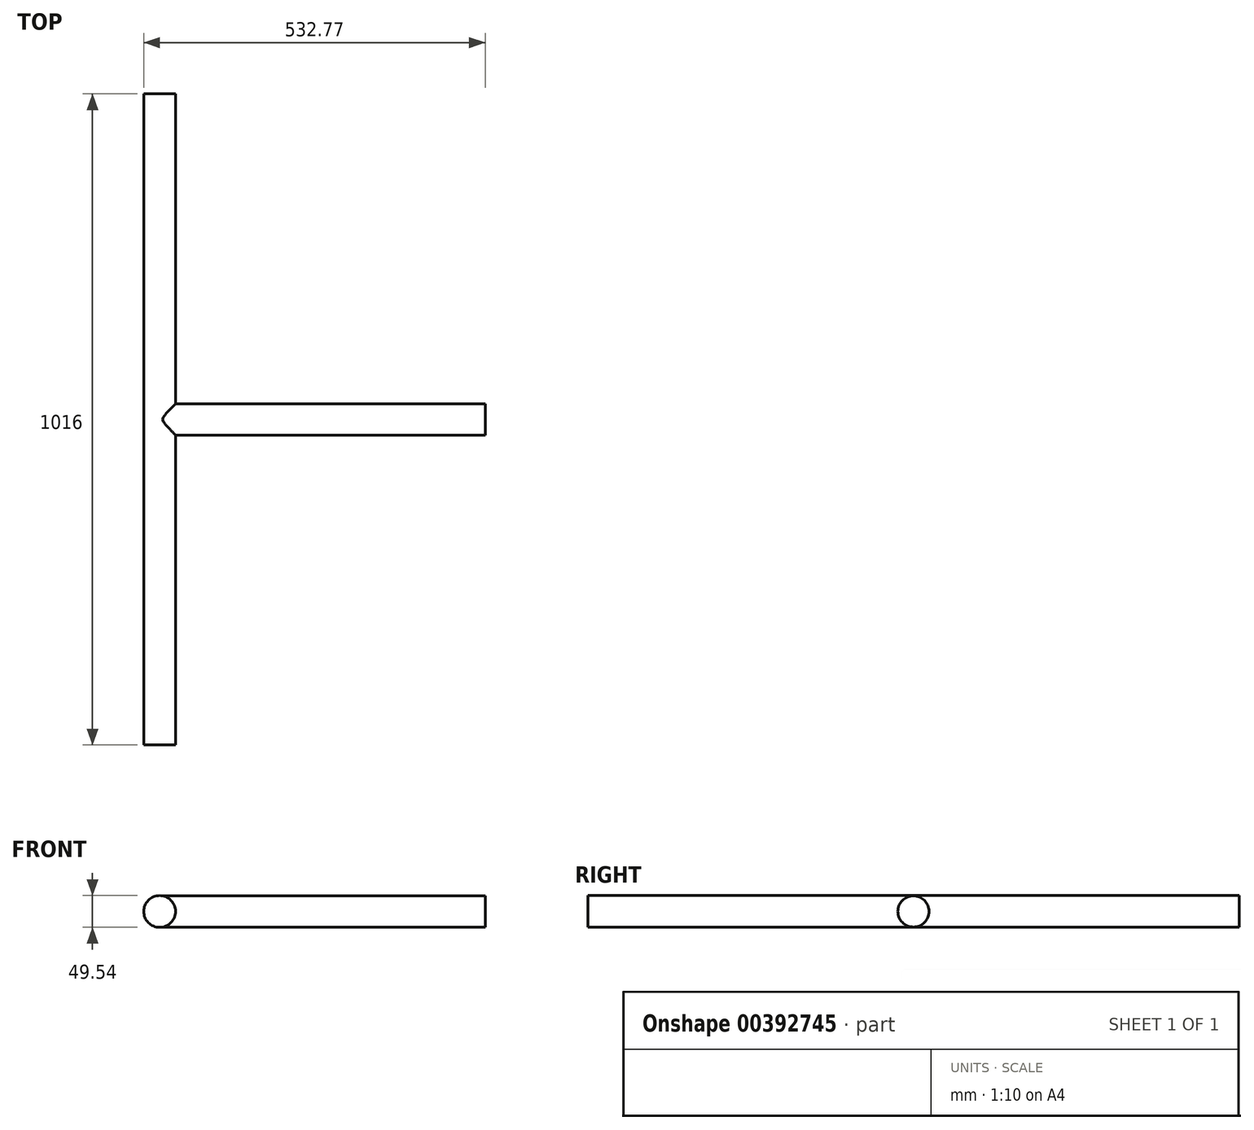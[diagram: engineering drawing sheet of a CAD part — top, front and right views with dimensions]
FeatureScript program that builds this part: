
annotation { "Feature Type Name" : "Feature", "Feature Type Description" : "" }
export const myFeature = defineFeature(function(context is Context, id is Id, definition is map)
    precondition{}
    {
        {
            var Q0;
            Q0=qCreatedBy(makeId("Front.planeOp"),FACE);
            var sketch = newSketch(context, id + "F0", { "sketchPlane" : qUnion([Q0])});
            skCircle(sketch, "E0", {"center": v(0, 0) * mm, "radius": 24.77 * mm});
            skSolve(sketch);
        }
        {
            var Q0;
            Q0 = qSketchRegion(id + "F0", true);
            extrude(context, id + "F1", {"entities" : qUnion([Q0]), "endBound" : BoundingType.SYMMETRIC, "depth" : 1016 * mm});
        }
        {
            var Q0;
            Q0=qCreatedBy(makeId("Right.planeOp"),FACE);
            var sketch = newSketch(context, id + "F2", { "sketchPlane" : qUnion([Q0])});
            skCircle(sketch, "E1", {"center": v(0, 0) * mm, "radius": 24.33 * mm});
            skSolve(sketch);
        }
        {
            var Q0;
            Q0 = qSketchRegion(id + "F2", true);
            extrude(context, id + "F3", {"entities" : qUnion([Q0]), "operationType" : NewBodyOperationType.ADD, "depth" : 508 * mm});
        }
    });
